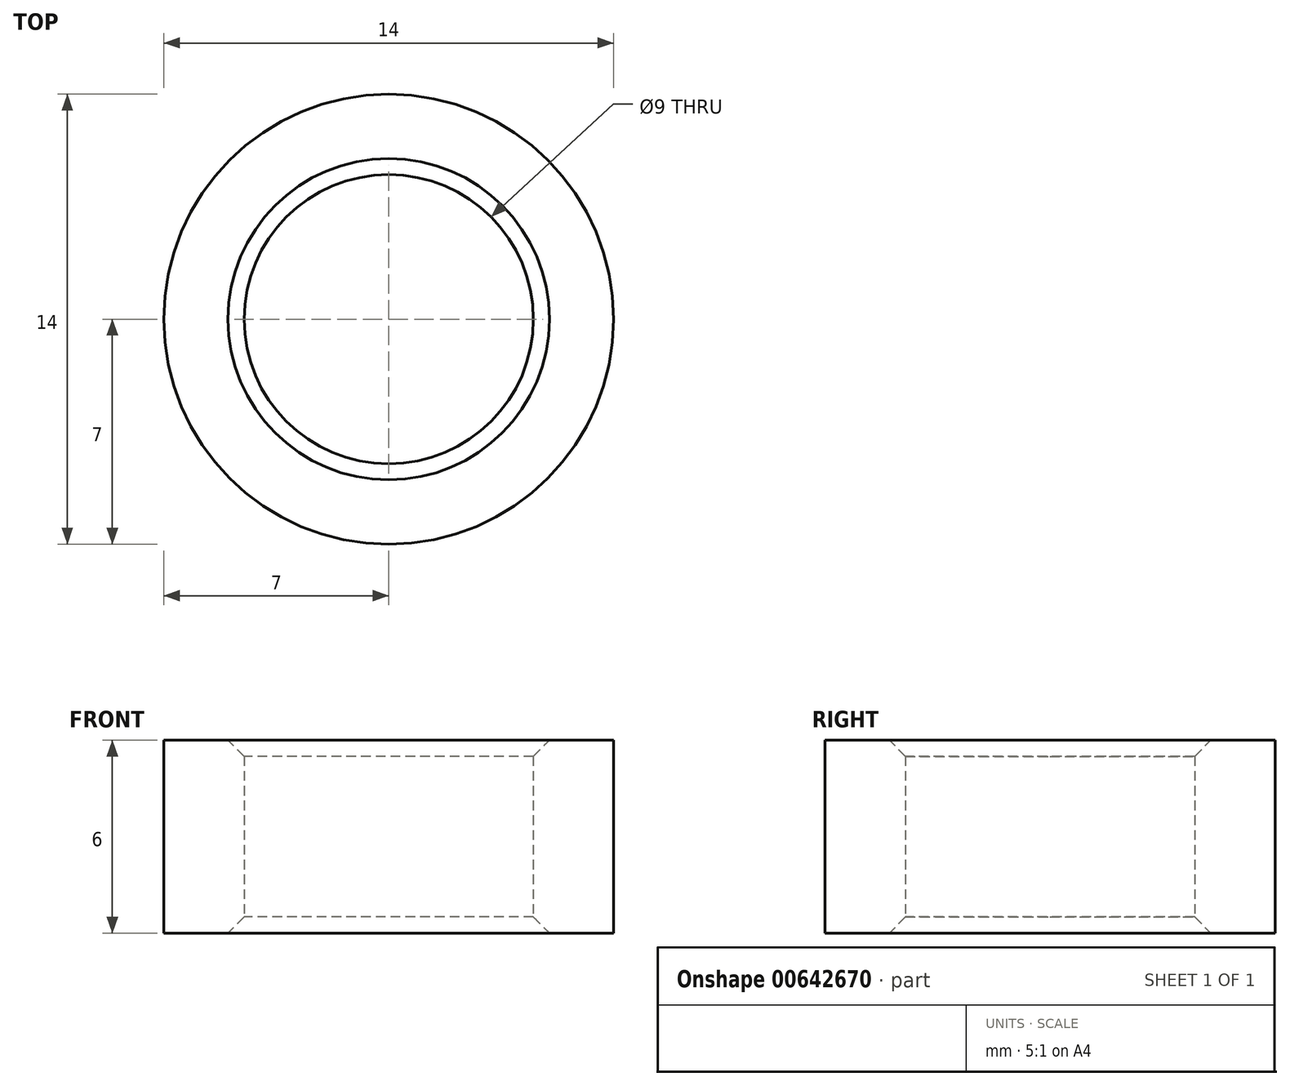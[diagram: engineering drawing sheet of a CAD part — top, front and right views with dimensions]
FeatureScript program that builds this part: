
annotation { "Feature Type Name" : "Feature", "Feature Type Description" : "" }
export const myFeature = defineFeature(function(context is Context, id is Id, definition is map)
    precondition{}
    {
        {
            var Q0;
            Q0=qCreatedBy(makeId("Top.planeOp"),FACE);
            var sketch = newSketch(context, id + "F0", { "sketchPlane" : qUnion([Q0])});
            skCircle(sketch, "E0", {"center": v(0, 0) * mm, "radius": 7 * mm});
            skCircle(sketch, "E1", {"center": v(0, 0) * mm, "radius": 4.5 * mm});
            skSolve(sketch);
        }
        {
            var Q0;
            Q0=makeQuery(id+"F0.imprint","IMPRINT",FACE,{"disambiguationData":[TD([[makeQuery(id+"F0.imprint","IMPRINT",EDGE,{"derivedFrom":sQuery(id+"F0.wireOp",EDGE,"E0")}),1.0]])]});
            extrude(context, id + "F1", {"entities" : qUnion([Q0]), "depth" : 6 * mm, "offsetDistance" : 25 * mm});
        }
        {
            var Q0;
            Q0=makeQuery(id+"F1.opExtrude","SWEPT_FACE",FACE,{"disambiguationData":[OSD([sQuery(id+"F0.wireOp",EDGE,"E1")])]});
            chamfer(context, id + "F2", {"entities" : qUnion([Q0]), "chamferType" : ChamferType.OFFSET_ANGLE, "width" : 0.5 * mm, "oppositeDirection" : false, "angle" : 45 * degree, "tangentPropagation" : true});
        }
    });
